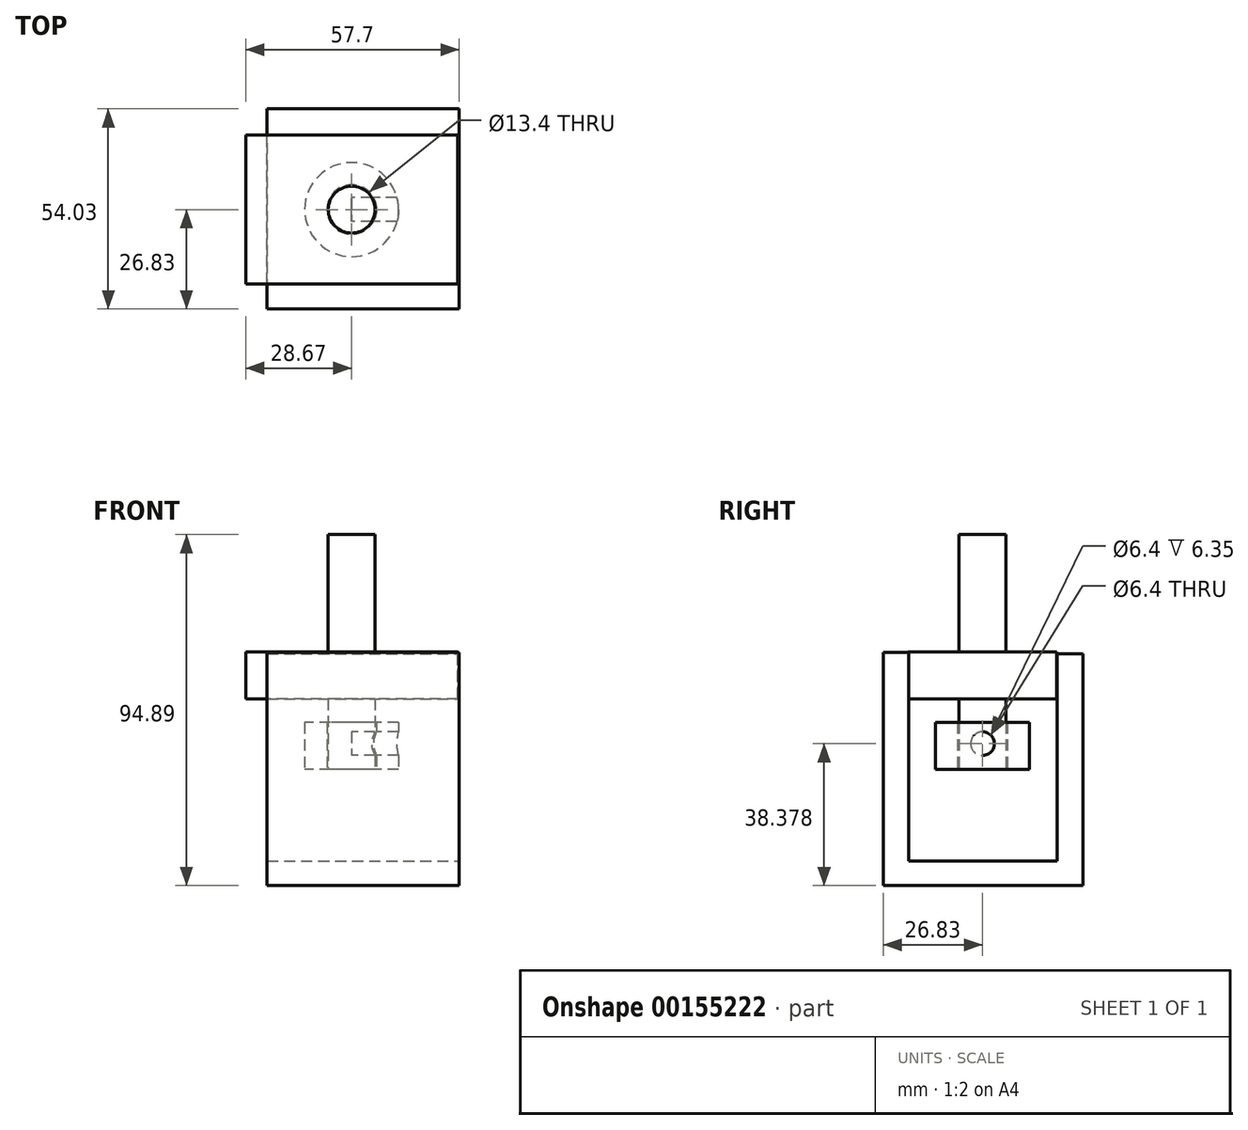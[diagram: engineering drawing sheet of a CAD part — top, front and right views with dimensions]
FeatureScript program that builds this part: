
annotation { "Feature Type Name" : "Feature", "Feature Type Description" : "" }
export const myFeature = defineFeature(function(context is Context, id is Id, definition is map)
    precondition{}
    {
        {
            var Q0;
            Q0=qCreatedBy(makeId("Top.planeOp"),FACE);
            var sketch = newSketch(context, id + "F0", { "sketchPlane" : qUnion([Q0])});
            skCircle(sketch, "E0", {"center": v(0, 0) * mm, "radius": 12.7 * mm});
            skCircle(sketch, "E1", {"center": v(0, 0) * mm, "radius": 6.7 * mm});
            skSolve(sketch);
        }
        {
            var Q0;
            Q0 = qSketchRegion(id + "F0", true);
            extrude(context, id + "F1", {"entities" : qUnion([Q0]), "depth" : 12.7 * mm});
        }
        {
            var Q0;
            Q0=qCreatedBy(makeId("Top.planeOp"),FACE);
            var sketch = newSketch(context, id + "F2", { "sketchPlane" : qUnion([Q0])});
            skCircle(sketch, "E2", {"center": v(0, 0) * mm, "radius": 6.35 * mm});
            skSolve(sketch);
        }
        {
            var Q0;
            Q0 = qSketchRegion(id + "F2", true);
            extrude(context, id + "F3", {"entities" : qUnion([Q0]), "depth" : 63.5 * mm});
        }
        {
            var Q0;
            Q0=qCreatedBy(makeId("Right.planeOp"),FACE);
            var sketch = newSketch(context, id + "F4", { "sketchPlane" : qUnion([Q0])});
            skCircle(sketch, "E3", {"center": v(0, 6.99) * mm, "radius": 3.26 * mm});
            skSolve(sketch);
        }
        {
            var Q0;
            Q0=sQuery(id+"F4.wireOp",VERTEX,"E3.center");
            var Q1;
            Q1=makeQuery(id+"F1.opExtrude","SWEPT_BODY",BODY,{"disambiguationData":[OSD([sQuery(id+"F0.wireOp",EDGE,"E0"),sQuery(id+"F0.wireOp",EDGE,"E1")])]});
            var Q2;
            Q2=makeQuery(id+"F3.opExtrude","SWEPT_BODY",BODY,{"disambiguationData":[OSD([sQuery(id+"F2.wireOp",EDGE,"E2")])]});
            hole(context, id + "F5", {"style" : HoleStyle.SIMPLE, "endStyle" : HoleEndStyle.THROUGH, "oppositeDirection" : true, "holeDiameter" : 0 * yard, "locations" : qUnion([Q0]), "scope" : qUnion([Q1, Q2]), "isTappedThrough" : true});
        }
        {
            var Q0;
            Q0=qCreatedBy(makeId("Top.planeOp"),FACE);
            cPlane(context, id + "F6", {"entities" : qUnion([Q0]), "cplaneType" : CPlaneType.OFFSET, "offset" : 19.05 * mm, "width" : 0.17 * yard, "height" : 0.17 * yard});
        }
        {
            var Q0;
            Q0=qCreatedBy(id+"F6.planeOp",FACE);
            var sketch = newSketch(context, id + "F7", { "sketchPlane" : qUnion([Q0])});
            skLineSegment(sketch, "E4.bottom", {"start": v(28.67, -20.1) * mm, "end": v(-28.67, -20.1) * mm});
            skLineSegment(sketch, "E4.top", {"start": v(28.67, 20.1) * mm, "end": v(-28.67, 20.1) * mm});
            skLineSegment(sketch, "E4.left", {"start": v(28.67, -20.1) * mm, "end": v(28.67, 20.1) * mm});
            skLineSegment(sketch, "E4.right", {"start": v(-28.67, -20.1) * mm, "end": v(-28.67, 20.1) * mm});
            skPoint(sketch, "E4.middle", {"position": v(0, 0) * mm});
            skCircle(sketch, "E5", {"center": v(0, 0) * mm, "radius": 6.35 * mm});
            skSolve(sketch);
        }
        {
            var Q0;
            Q0=makeQuery(id+"F7.imprint","IMPRINT",FACE,{"disambiguationData":[TD([[makeQuery(id+"F7.imprint","IMPRINT",EDGE,{"derivedFrom":sQuery(id+"F7.wireOp",EDGE,"E4.bottom")}),-1.0]])]});
            extrude(context, id + "F8", {"entities" : qUnion([Q0]), "operationType" : NewBodyOperationType.ADD, "depth" : 12.7 * mm});
        }
        {
            var Q0;
            Q0=makeQuery(id+"F8.opExtrude","CAP_FACE",FACE,{"disambiguationData":[OSD([sQuery(id+"F7.wireOp",EDGE,"E4.bottom"),sQuery(id+"F7.wireOp",EDGE,"E4.top"),sQuery(id+"F7.wireOp",EDGE,"E4.left"),sQuery(id+"F7.wireOp",EDGE,"E4.right"),sQuery(id+"F7.wireOp",EDGE,"E5")])],"isStart":false});
            var sketch = newSketch(context, id + "F9", { "sketchPlane" : qUnion([Q0])});
            skCircle(sketch, "E6", {"center": v(0, 0) * mm, "radius": 8.86 * mm});
            skSolve(sketch);
        }
        {
            var Q0;
            Q0=qCreatedBy(makeId("Right.planeOp"),FACE);
            var sketch = newSketch(context, id + "F10", { "sketchPlane" : qUnion([Q0])});
            skLineSegment(sketch, "E7.bottom", {"start": v(-20.01, 31.62) * mm, "end": v(-26.83, 31.62) * mm});
            skLineSegment(sketch, "E7.top", {"start": v(-20.01, -31.4) * mm, "end": v(-26.83, -31.4) * mm});
            skLineSegment(sketch, "E7.left", {"start": v(-20.01, 31.62) * mm, "end": v(-20.01, -24.7) * mm});
            skLineSegment(sketch, "E7.right", {"start": v(-26.83, 31.62) * mm, "end": v(-26.83, -31.4) * mm});
            skLineSegment(sketch, "E8.bottom", {"start": v(-20.01, -31.4) * mm, "end": v(27.2, -31.4) * mm});
            skLineSegment(sketch, "E8.top", {"start": v(-20.01, -24.7) * mm, "end": v(20.14, -24.7) * mm});
            skLineSegment(sketch, "E8.right", {"start": v(27.2, -31.4) * mm, "end": v(27.2, -24.7) * mm});
            skLineSegment(sketch, "E9.bottom", {"start": v(20.14, 31.25) * mm, "end": v(27.2, 31.25) * mm});
            skLineSegment(sketch, "E9.left", {"start": v(20.14, 31.25) * mm, "end": v(20.14, -24.7) * mm});
            skLineSegment(sketch, "E10", {"start": v(27.2, 31.25) * mm, "end": v(27.2, -24.7) * mm});
            skSolve(sketch);
        }
        {
            var Q0;
            Q0=makeQuery(id+"F10.imprint","IMPRINT",FACE,{"disambiguationData":[TD([[makeQuery(id+"F10.imprint","IMPRINT",EDGE,{"derivedFrom":sQuery(id+"F10.wireOp",EDGE,"E7.bottom")}),1.0]])]});
            var Q1;
            Q1=sQuery(id+"F10.wireOp",EDGE,"E8.bottom");
            extrude(context, id + "F11", {"entities" : qUnion([Q0]), "operationType" : NewBodyOperationType.ADD, "surfaceEntities" : qUnion([Q1]), "oppositeDirection" : true, "depth" : 0.02 * yard, "hasSecondDirection" : true, "secondDirectionOppositeDirection" : false, "secondDirectionDepth" : 0.03 * yard});
        }
    });
